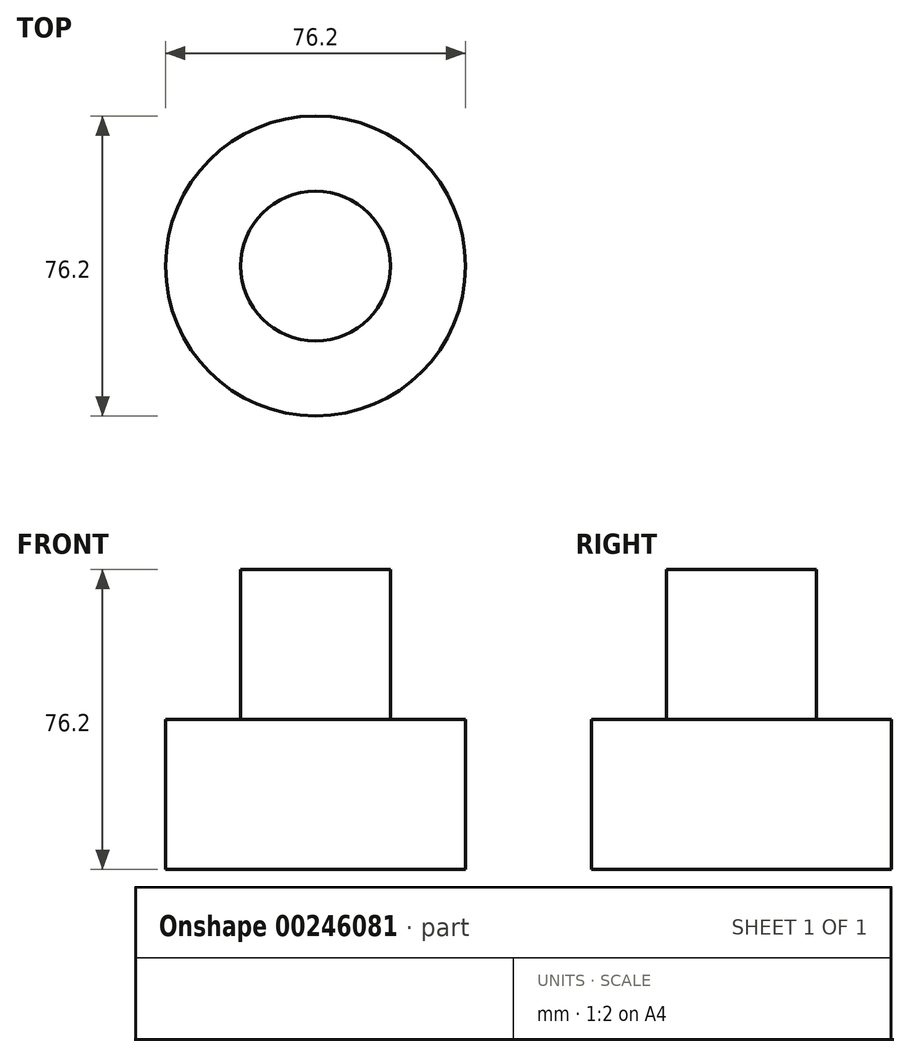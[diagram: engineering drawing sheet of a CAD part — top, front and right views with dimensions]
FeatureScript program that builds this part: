
annotation { "Feature Type Name" : "Feature", "Feature Type Description" : "" }
export const myFeature = defineFeature(function(context is Context, id is Id, definition is map)
    precondition{}
    {
        {
            var Q0;
            Q0=qCreatedBy(makeId("Front.planeOp"),FACE);
            var sketch = newSketch(context, id + "F0", { "sketchPlane" : qUnion([Q0])});
            skLineSegment(sketch, "E0", {"start": v(0, 0) * mm, "end": v(-38.1, 0) * mm});
            skLineSegment(sketch, "E1", {"start": v(-38.1, 0) * mm, "end": v(-38.1, 38.1) * mm});
            skLineSegment(sketch, "E2", {"start": v(-38.1, 38.1) * mm, "end": v(-19.05, 38.1) * mm});
            skLineSegment(sketch, "E3", {"start": v(-19.05, 38.1) * mm, "end": v(-19.05, 76.2) * mm});
            skLineSegment(sketch, "E4", {"start": v(-19.05, 76.2) * mm, "end": v(0, 76.2) * mm});
            skLineSegment(sketch, "E5", {"start": v(0, 76.2) * mm, "end": v(0, 0) * mm});
            skSolve(sketch);
        }
        {
            var Q0;
            Q0=makeQuery(id+"F0.imprint","IMPRINT",FACE,{"disambiguationData":[TD([[makeQuery(id+"F0.imprint","IMPRINT",EDGE,{"derivedFrom":sQuery(id+"F0.wireOp",EDGE,"E0")}),-1.0]])]});
            var Q1;
            Q1=sQuery(id+"F0.wireOp",EDGE,"E5");
            revolve(context, id + "F1", {"entities" : qUnion([Q0]), "axis" : qUnion([Q1]), "revolveType" : RevolveType.FULL});
        }
    });
